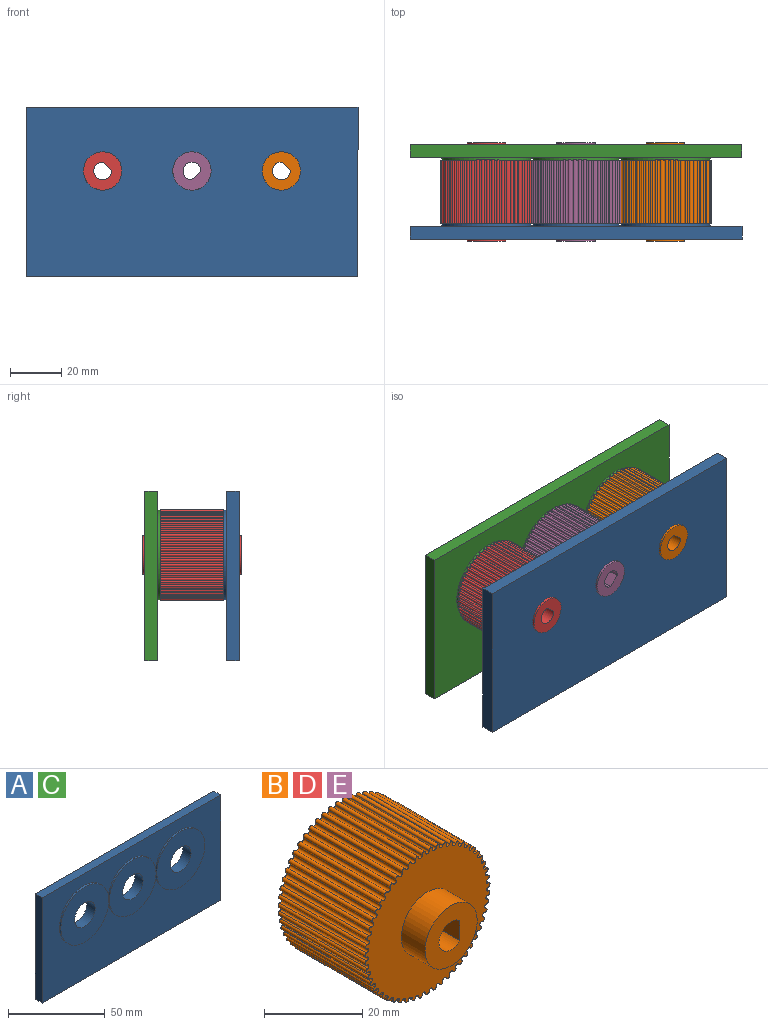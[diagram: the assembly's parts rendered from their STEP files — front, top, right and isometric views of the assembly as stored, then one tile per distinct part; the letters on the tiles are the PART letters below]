
ASSEMBLY  parts=5 mates=6
PART A: 15 faces, bbox 130x6x66.5 mm
  f0: plane 66.47x5mm, normal (-1,0,0), area 332.3mm2, adj f1,f5,f7,f8
  f1: plane 130x5mm, normal (0,0,-1), area 650mm2, adj f0,f2,f7,f8
  f2: plane 66.47x5mm, normal (1,0,0), area 332.3mm2, adj f1,f5,f7,f8
  f3: cylinder r=7.5mm len=15mm, axis (0,1,0), area 282.7mm2, adj f8,f14
  f4: cylinder r=7.5mm len=15mm, axis (0,1,0), area 282.7mm2, adj f8,f10
  f5: plane 130x5mm, normal (0,0,1), area 650mm2, adj f0,f2,f7,f8
  f6: cylinder r=7.5mm len=15mm, axis (0,1,0), area 282.7mm2, adj f8,f12
  f7: plane 130x66.47mm, normal (0,-1,0), area 5808.4mm2, adj f0,f1,f2,f5,f9,f11,f13
  f8: plane 130x66.47mm, normal (0,1,0), area 8110.4mm2, adj f0,f1,f2,f3,f4,f5,f6
  f9: cylinder r=17.5mm len=35mm, axis (0,1,0), area 110mm2, adj f7,f10
  f10: plane 35x35mm, normal (0,-1,0), area 785.4mm2, adj f4,f9
  f11: cylinder r=17.5mm len=35mm, axis (0,1,0), area 110mm2, adj f7,f12
  f12: plane 35x35mm, normal (0,-1,0), area 785.4mm2, adj f6,f11
  f13: cylinder r=17mm len=34mm, axis (0,1,0), area 106.8mm2, adj f7,f14
  f14: plane 34x34mm, normal (0,-1,0), area 731.2mm2, adj f3,f13
PART B: 118 faces, bbox 36x38.6x36 mm
  f0: plane 15x15mm, normal (0,-1,0), area 141.6mm2, adj f114,f116,f117
  f1: plane 15x15mm, normal (0,1,0), area 141.6mm2, adj f115,f116,f117
  f2: cylinder r=0.5mm len=25mm, axis (0,1,0), area 39.6mm2, adj f3,f4,f51,f52
  f3: plane 35.99x35.97mm, normal (0,-1,0), area 785.7mm2, adj f2,f5,f6,f7,f8,f9,f10,f11
  f4: plane 35.99x35.97mm, normal (0,1,0), area 785.7mm2, adj f2,f5,f6,f7,f8,f9,f10,f11
  f5: cylinder r=0.5mm len=25mm, axis (0,1,0), area 39.6mm2, adj f3,f4,f46,f47
  f6: cylinder r=0.5mm len=25mm, axis (0,1,0), area 39.6mm2, adj f3,f4,f47,f48
  f7: cylinder r=0.5mm len=25mm, axis (0,1,0), area 39.6mm2, adj f3,f4,f45,f46
  f8: cylinder r=0.5mm len=25mm, axis (0,1,0), area 39.6mm2, adj f3,f4,f48,f49
  f9: cylinder r=0.5mm len=25mm, axis (0,1,0), area 39.6mm2, adj f3,f4,f52,f53
  f10: cylinder r=0.5mm len=25mm, axis (0,1,0), area 39.6mm2, adj f3,f4,f49,f50
  f11: cylinder r=0.5mm len=25mm, axis (0,1,0), area 39.6mm2, adj f3,f4,f50,f51
  f12: cylinder r=0.5mm len=25mm, axis (0,1,0), area 39.6mm2, adj f3,f4,f43,f44
  f13: cylinder r=0.5mm len=25mm, axis (0,1,0), area 39.6mm2, adj f3,f4,f14,f15
  f14: cylinder r=0.5mm len=25mm, axis (0,1,0), area 38.9mm2, adj f3,f4,f13,f17
  f15: cylinder r=0.5mm len=25mm, axis (0,1,0), area 38.9mm2, adj f3,f4,f13,f16
  f16: cylinder r=0.5mm len=25mm, axis (0,1,0), area 39.6mm2, adj f3,f4,f15,f44
  f17: cylinder r=0.5mm len=25mm, axis (0,1,0), area 39.6mm2, adj f3,f4,f14,f45
  f18: cylinder r=0.5mm len=25mm, axis (0,1,0), area 38.9mm2, adj f3,f4,f95,f96
  f19: cylinder r=0.5mm len=25mm, axis (0,1,0), area 38.9mm2, adj f3,f4,f94,f95
  f20: cylinder r=0.5mm len=25mm, axis (0,1,0), area 38.9mm2, adj f3,f4,f93,f94
  f21: cylinder r=0.5mm len=25mm, axis (0,1,0), area 38.9mm2, adj f3,f4,f92,f93
  f22: cylinder r=0.5mm len=25mm, axis (0,1,0), area 38.9mm2, adj f3,f4,f91,f92
  f23: cylinder r=0.5mm len=25mm, axis (0,1,0), area 38.9mm2, adj f3,f4,f90,f91
  f24: cylinder r=0.5mm len=25mm, axis (0,1,0), area 38.9mm2, adj f3,f4,f89,f90
  f25: cylinder r=0.5mm len=25mm, axis (0,1,0), area 38.9mm2, adj f3,f4,f88,f89
  f26: cylinder r=0.5mm len=25mm, axis (0,1,0), area 38.9mm2, adj f3,f4,f87,f88
  f27: cylinder r=0.5mm len=25mm, axis (0,1,0), area 38.9mm2, adj f3,f4,f86,f87
  f28: cylinder r=0.5mm len=25mm, axis (0,1,0), area 38.9mm2, adj f3,f4,f85,f86
  f29: cylinder r=0.5mm len=25mm, axis (0,1,0), area 38.9mm2, adj f3,f4,f84,f85
  f30: cylinder r=0.5mm len=25mm, axis (0,1,0), area 38.9mm2, adj f3,f4,f83,f84
  f31: cylinder r=0.5mm len=25mm, axis (0,1,0), area 38.9mm2, adj f3,f4,f82,f83
  f32: cylinder r=0.5mm len=25mm, axis (0,1,0), area 38.9mm2, adj f3,f4,f81,f82
  f33: cylinder r=0.5mm len=25mm, axis (0,1,0), area 38.9mm2, adj f3,f4,f80,f81
  f34: cylinder r=0.5mm len=25mm, axis (0,1,0), area 38.9mm2, adj f3,f4,f79,f80
  f35: cylinder r=0.5mm len=25mm, axis (0,1,0), area 38.9mm2, adj f3,f4,f78,f79
  f36: cylinder r=0.5mm len=25mm, axis (0,1,0), area 38.9mm2, adj f3,f4,f77,f78
  f37: cylinder r=0.5mm len=25mm, axis (0,1,0), area 38.9mm2, adj f3,f4,f76,f77
  f38: cylinder r=0.5mm len=25mm, axis (0,1,0), area 38.9mm2, adj f3,f4,f75,f76
  f39: cylinder r=0.5mm len=25mm, axis (0,1,0), area 38.9mm2, adj f3,f4,f71,f75
  f40: cylinder r=0.5mm len=25mm, axis (0,1,0), area 38.9mm2, adj f3,f4,f71,f72
  f41: cylinder r=0.5mm len=25mm, axis (0,1,0), area 38.9mm2, adj f3,f4,f72,f74
  f42: cylinder r=0.5mm len=25mm, axis (0,1,0), area 38.9mm2, adj f3,f4,f73,f74
  f43: cylinder r=0.5mm len=25mm, axis (0,1,0), area 38.9mm2, adj f3,f4,f12,f73
  f44: cylinder r=0.5mm len=25mm, axis (0,1,0), area 38.9mm2, adj f3,f4,f12,f16
  f45: cylinder r=0.5mm len=25mm, axis (0,1,0), area 38.9mm2, adj f3,f4,f7,f17
  f46: cylinder r=0.5mm len=25mm, axis (0,1,0), area 38.9mm2, adj f3,f4,f5,f7
  f47: cylinder r=0.5mm len=25mm, axis (0,1,0), area 38.9mm2, adj f3,f4,f5,f6
  f48: cylinder r=0.5mm len=25mm, axis (0,1,0), area 38.9mm2, adj f3,f4,f6,f8
  f49: cylinder r=0.5mm len=25mm, axis (0,1,0), area 38.9mm2, adj f3,f4,f8,f10
  f50: cylinder r=0.5mm len=25mm, axis (0,1,0), area 38.9mm2, adj f3,f4,f10,f11
  f51: cylinder r=0.5mm len=25mm, axis (0,1,0), area 38.9mm2, adj f2,f3,f4,f11
  f52: cylinder r=0.5mm len=25mm, axis (0,1,0), area 38.9mm2, adj f2,f3,f4,f9
  f53: cylinder r=0.5mm len=25mm, axis (0,1,0), area 38.9mm2, adj f3,f4,f9,f113
  f54: cylinder r=0.5mm len=25mm, axis (0,1,0), area 38.9mm2, adj f3,f4,f112,f113
  f55: cylinder r=0.5mm len=25mm, axis (0,1,0), area 38.9mm2, adj f3,f4,f111,f112
  f56: cylinder r=0.5mm len=25mm, axis (0,1,0), area 38.9mm2, adj f3,f4,f110,f111
  f57: cylinder r=0.5mm len=25mm, axis (0,1,0), area 38.9mm2, adj f3,f4,f109,f110
  f58: cylinder r=0.5mm len=25mm, axis (0,1,0), area 38.9mm2, adj f3,f4,f108,f109
  f59: cylinder r=0.5mm len=25mm, axis (0,1,0), area 38.9mm2, adj f3,f4,f107,f108
  f60: cylinder r=0.5mm len=25mm, axis (0,1,0), area 38.9mm2, adj f3,f4,f106,f107
  f61: cylinder r=0.5mm len=25mm, axis (0,1,0), area 38.9mm2, adj f3,f4,f105,f106
  f62: cylinder r=0.5mm len=25mm, axis (0,1,0), area 38.9mm2, adj f3,f4,f104,f105
  f63: cylinder r=0.5mm len=25mm, axis (0,1,0), area 38.9mm2, adj f3,f4,f103,f104
  f64: cylinder r=0.5mm len=25mm, axis (0,1,0), area 38.9mm2, adj f3,f4,f102,f103
  f65: cylinder r=0.5mm len=25mm, axis (0,1,0), area 38.9mm2, adj f3,f4,f101,f102
  f66: cylinder r=0.5mm len=25mm, axis (0,1,0), area 38.9mm2, adj f3,f4,f100,f101
  f67: cylinder r=0.5mm len=25mm, axis (0,1,0), area 38.9mm2, adj f3,f4,f99,f100
  f68: cylinder r=0.5mm len=25mm, axis (0,1,0), area 38.9mm2, adj f3,f4,f98,f99
  f69: cylinder r=0.5mm len=25mm, axis (0,1,0), area 38.9mm2, adj f3,f4,f97,f98
  f70: cylinder r=0.5mm len=25mm, axis (0,1,0), area 38.9mm2, adj f3,f4,f96,f97
  f71: cylinder r=0.5mm len=25mm, axis (0,1,0), area 39.6mm2, adj f3,f4,f39,f40
  f72: cylinder r=0.5mm len=25mm, axis (0,1,0), area 39.6mm2, adj f3,f4,f40,f41
  f73: cylinder r=0.5mm len=25mm, axis (0,1,0), area 39.6mm2, adj f3,f4,f42,f43
  f74: cylinder r=0.5mm len=25mm, axis (0,1,0), area 39.6mm2, adj f3,f4,f41,f42
  f75: cylinder r=0.5mm len=25mm, axis (0,1,0), area 39.6mm2, adj f3,f4,f38,f39
  f76: cylinder r=0.5mm len=25mm, axis (0,1,0), area 39.6mm2, adj f3,f4,f37,f38
  f77: cylinder r=0.5mm len=25mm, axis (0,1,0), area 39.6mm2, adj f3,f4,f36,f37
  f78: cylinder r=0.5mm len=25mm, axis (0,1,0), area 39.6mm2, adj f3,f4,f35,f36
  f79: cylinder r=0.5mm len=25mm, axis (0,1,0), area 39.6mm2, adj f3,f4,f34,f35
  f80: cylinder r=0.5mm len=25mm, axis (0,1,0), area 39.6mm2, adj f3,f4,f33,f34
  f81: cylinder r=0.5mm len=25mm, axis (0,1,0), area 39.6mm2, adj f3,f4,f32,f33
  f82: cylinder r=0.5mm len=25mm, axis (0,1,0), area 39.6mm2, adj f3,f4,f31,f32
  f83: cylinder r=0.5mm len=25mm, axis (0,1,0), area 39.6mm2, adj f3,f4,f30,f31
  f84: cylinder r=0.5mm len=25mm, axis (0,1,0), area 39.6mm2, adj f3,f4,f29,f30
  f85: cylinder r=0.5mm len=25mm, axis (0,1,0), area 39.6mm2, adj f3,f4,f28,f29
  f86: cylinder r=0.5mm len=25mm, axis (0,1,0), area 39.6mm2, adj f3,f4,f27,f28
  f87: cylinder r=0.5mm len=25mm, axis (0,1,0), area 39.6mm2, adj f3,f4,f26,f27
  f88: cylinder r=0.5mm len=25mm, axis (0,1,0), area 39.6mm2, adj f3,f4,f25,f26
  f89: cylinder r=0.5mm len=25mm, axis (0,1,0), area 39.6mm2, adj f3,f4,f24,f25
  f90: cylinder r=0.5mm len=25mm, axis (0,1,0), area 39.6mm2, adj f3,f4,f23,f24
  f91: cylinder r=0.5mm len=25mm, axis (0,1,0), area 39.6mm2, adj f3,f4,f22,f23
  f92: cylinder r=0.5mm len=25mm, axis (0,1,0), area 39.6mm2, adj f3,f4,f21,f22
  f93: cylinder r=0.5mm len=25mm, axis (0,1,0), area 39.6mm2, adj f3,f4,f20,f21
  f94: cylinder r=0.5mm len=25mm, axis (0,1,0), area 39.6mm2, adj f3,f4,f19,f20
  f95: cylinder r=0.5mm len=25mm, axis (0,1,0), area 39.6mm2, adj f3,f4,f18,f19
  f96: cylinder r=0.5mm len=25mm, axis (0,1,0), area 39.6mm2, adj f3,f4,f18,f70
  f97: cylinder r=0.5mm len=25mm, axis (0,1,0), area 39.6mm2, adj f3,f4,f69,f70
  f98: cylinder r=0.5mm len=25mm, axis (0,1,0), area 39.6mm2, adj f3,f4,f68,f69
  f99: cylinder r=0.5mm len=25mm, axis (0,1,0), area 39.6mm2, adj f3,f4,f67,f68
  f100: cylinder r=0.5mm len=25mm, axis (0,1,0), area 39.6mm2, adj f3,f4,f66,f67
  f101: cylinder r=0.5mm len=25mm, axis (0,1,0), area 39.6mm2, adj f3,f4,f65,f66
  f102: cylinder r=0.5mm len=25mm, axis (0,1,0), area 39.6mm2, adj f3,f4,f64,f65
  f103: cylinder r=0.5mm len=25mm, axis (0,1,0), area 39.6mm2, adj f3,f4,f63,f64
  f104: cylinder r=0.5mm len=25mm, axis (0,1,0), area 39.6mm2, adj f3,f4,f62,f63
  f105: cylinder r=0.5mm len=25mm, axis (0,1,0), area 39.6mm2, adj f3,f4,f61,f62
  f106: cylinder r=0.5mm len=25mm, axis (0,1,0), area 39.6mm2, adj f3,f4,f60,f61
  f107: cylinder r=0.5mm len=25mm, axis (0,1,0), area 39.6mm2, adj f3,f4,f59,f60
  f108: cylinder r=0.5mm len=25mm, axis (0,1,0), area 39.6mm2, adj f3,f4,f58,f59
  f109: cylinder r=0.5mm len=25mm, axis (0,1,0), area 39.6mm2, adj f3,f4,f57,f58
  f110: cylinder r=0.5mm len=25mm, axis (0,1,0), area 39.6mm2, adj f3,f4,f56,f57
  f111: cylinder r=0.5mm len=25mm, axis (0,1,0), area 39.6mm2, adj f3,f4,f55,f56
  f112: cylinder r=0.5mm len=25mm, axis (0,1,0), area 39.6mm2, adj f3,f4,f54,f55
  f113: cylinder r=0.5mm len=25mm, axis (0,1,0), area 39.6mm2, adj f3,f4,f53,f54
  f114: cylinder r=7.5mm len=15mm, axis (0,1,0), area 320.4mm2, adj f0,f3
  f115: cylinder r=7.5mm len=15mm, axis (0,-1,0), area 320.4mm2, adj f1,f4
  f116: cylinder r=3.5mm len=38.6mm, axis (0,1,0), area 639.4mm2, adj f0,f1,f117
  f117: plane 38.6x4.9mm, normal (-1,0,0), area 189.1mm2, adj f0,f1,f116
PART C: same geometry as A
PART D: same geometry as B
PART E: same geometry as B
PLACE A rot(axis=(0,0,-1),180deg) t=(0,-37,0)mm
PLACE B rot(axis=(0,-1,0),47.4deg) t=(35,-6,8.23)mm
PLACE C at identity fixed
PLACE D rot(axis=(0,-1,0),47.4deg) t=(-35,-6,8.23)mm
PLACE E rot(axis=(0,1,0),47.4deg) t=(0,-6,8.23)mm
MATE revolute C.f6 <-> D.f114  axis (0,-1,0) through (-35,-6,8.23)mm
MATE revolute A.f6 <-> B.f114  axis (0,1,0) through (35,-31,8.23)mm
MATE revolute C.f3 <-> E.f114  axis (0,-1,0) through (0,-6,8.23)mm
MATE revolute D.f114 <-> A.f4  axis (0,1,0) through (-35,-31,8.23)mm
MATE revolute C.f4 <-> B.f114  axis (0,-1,0) through (35,-6,8.23)mm
MATE revolute A.f3 <-> E.f114  axis (0,1,0) through (0,-31,8.23)mm
